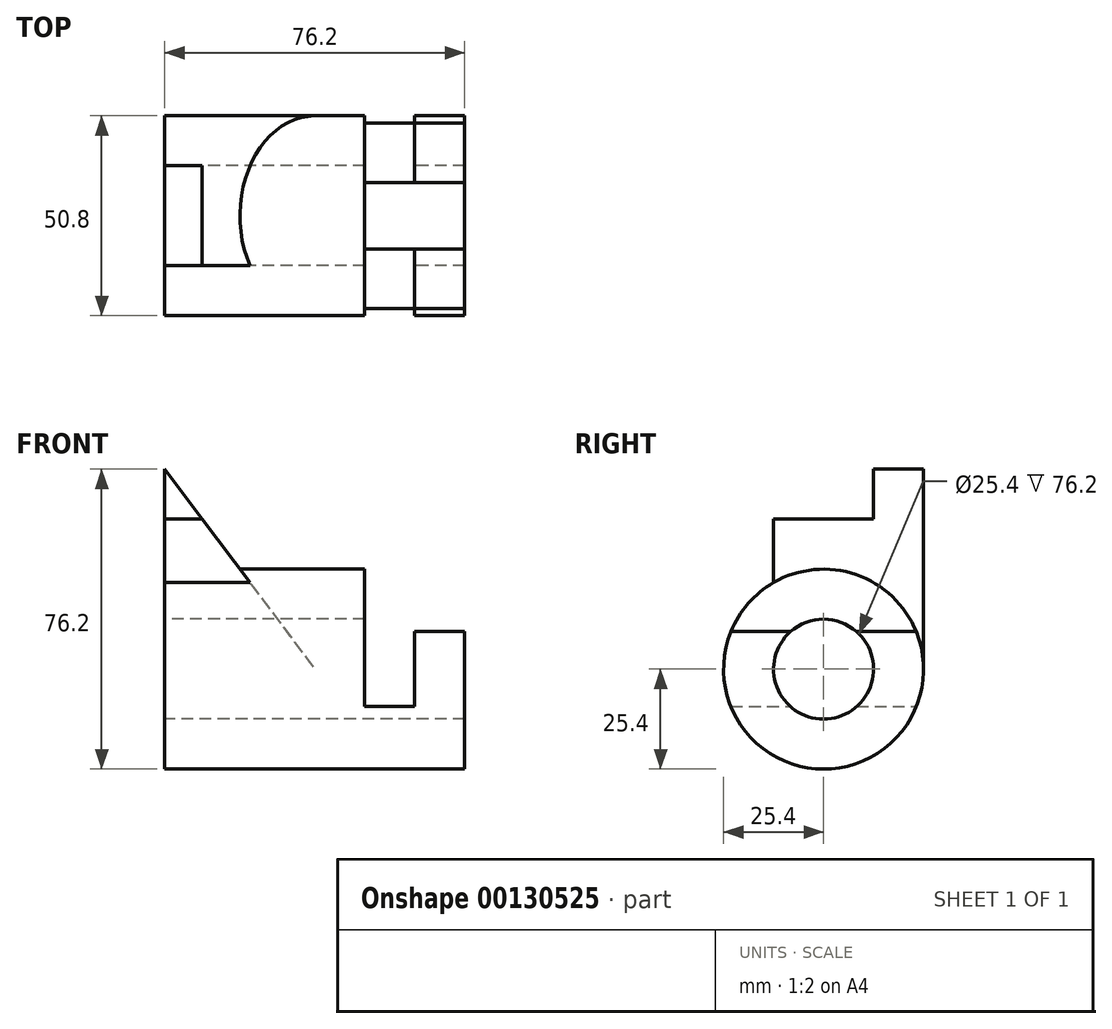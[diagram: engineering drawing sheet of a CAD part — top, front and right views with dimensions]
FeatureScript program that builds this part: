
annotation { "Feature Type Name" : "Feature", "Feature Type Description" : "" }
export const myFeature = defineFeature(function(context is Context, id is Id, definition is map)
    precondition{}
    {
        {
            var Q0;
            Q0=qCreatedBy(makeId("Right.planeOp"),FACE);
            var sketch = newSketch(context, id + "F0", { "sketchPlane" : qUnion([Q0])});
            skCircle(sketch, "E0", {"center": v(0, 0) * mm, "radius": 12.7 * mm});
            skCircle(sketch, "E1", {"center": v(0, 0) * mm, "radius": 25.4 * mm});
            skSolve(sketch);
        }
        {
            var Q0;
            Q0=makeQuery(id+"F0.imprint","IMPRINT",FACE,{"disambiguationData":[TD([[makeQuery(id+"F0.imprint","IMPRINT",EDGE,{"derivedFrom":sQuery(id+"F0.wireOp",EDGE,"E0")}),-1.0]])]});
            extrude(context, id + "F1", {"entities" : qUnion([Q0]), "depth" : 76.2 * mm});
        }
        {
            var Q0;
            Q0=qCreatedBy(makeId("Front.planeOp"),FACE);
            var sketch = newSketch(context, id + "F2", { "sketchPlane" : qUnion([Q0])});
            skLineSegment(sketch, "E2", {"start": v(50.8, 25.4) * mm, "end": v(50.8, -9.53) * mm});
            skLineSegment(sketch, "E3", {"start": v(50.8, -9.53) * mm, "end": v(63.5, -9.52) * mm});
            skLineSegment(sketch, "E4", {"start": v(63.5, -9.52) * mm, "end": v(63.5, 9.53) * mm});
            skLineSegment(sketch, "E5", {"start": v(63.5, 9.53) * mm, "end": v(76.2, 9.53) * mm});
            skLineSegment(sketch, "E6", {"start": v(76.2, 9.53) * mm, "end": v(76.2, 25.4) * mm});
            skLineSegment(sketch, "E7", {"start": v(76.2, 25.4) * mm, "end": v(50.8, 25.4) * mm});
            skLineSegment(sketch, "E8", {"start": v(25.4, 25.4) * mm, "end": v(76.2, 25.4) * mm});
            skLineSegment(sketch, "E9", {"start": v(76.2, -25.4) * mm, "end": v(0, -25.4) * mm});
            skSolve(sketch);
        }
        {
            var Q0;
            Q0=makeQuery(id+"F0.imprint","IMPRINT",FACE,{"disambiguationData":[TD([[makeQuery(id+"F0.imprint","IMPRINT",EDGE,{"derivedFrom":sQuery(id+"F0.wireOp",EDGE,"E0")}),1.0]])]});
            extrude(context, id + "F3", {"entities" : qUnion([Q0]), "operationType" : NewBodyOperationType.REMOVE, "depth" : 76.2 * mm});
        }
        {
            var Q0;
            Q0=qCreatedBy(makeId("Front.planeOp"),FACE);
            var sketch = newSketch(context, id + "F4", { "sketchPlane" : qUnion([Q0])});
            skLineSegment(sketch, "E10", {"start": v(0, 0) * mm, "end": v(0, 50.8) * mm});
            skLineSegment(sketch, "E11", {"start": v(0, 50.8) * mm, "end": v(38.1, 0) * mm});
            skLineSegment(sketch, "E12", {"start": v(0, 0) * mm, "end": v(38.1, 0) * mm});
            skSolve(sketch);
        }
        {
            var Q0;
            Q0 = qSketchRegion(id + "F2", true);
            extrude(context, id + "F5", {"entities" : qUnion([Q0]), "operationType" : NewBodyOperationType.REMOVE, "endBound" : BoundingType.SYMMETRIC, "depth" : 50.8 * mm});
        }
        {
            var Q0;
            Q0=makeQuery(id+"F4.imprint","IMPRINT",FACE,{"disambiguationData":[TD([[makeQuery(id+"F4.imprint","IMPRINT",EDGE,{"derivedFrom":sQuery(id+"F4.wireOp",EDGE,"E10")}),-1.0]])]});
            extrude(context, id + "F6", {"entities" : qUnion([Q0]), "operationType" : NewBodyOperationType.ADD, "oppositeDirection" : true, "depth" : 25.4 * mm});
        }
        {
            var Q0;
            Q0 = qSketchRegion(id + "F4", true);
            extrude(context, id + "F7", {"entities" : qUnion([Q0]), "operationType" : NewBodyOperationType.ADD, "depth" : 12.7 * mm});
        }
        {
            var Q0;
            Q0=qCreatedBy(makeId("Right.planeOp"),FACE);
            var sketch = newSketch(context, id + "F8", { "sketchPlane" : qUnion([Q0])});
            skLineSegment(sketch, "E13.bottom", {"start": v(-12.7, 38.1) * mm, "end": v(12.7, 38.1) * mm});
            skLineSegment(sketch, "E13.top", {"start": v(-12.7, 50.8) * mm, "end": v(12.7, 50.8) * mm});
            skLineSegment(sketch, "E13.left", {"start": v(-12.7, 38.1) * mm, "end": v(-12.7, 50.8) * mm});
            skLineSegment(sketch, "E13.right", {"start": v(12.7, 38.1) * mm, "end": v(12.7, 50.8) * mm});
            skSolve(sketch);
        }
        {
            var Q0;
            Q0 = qSketchRegion(id + "F8", true);
            extrude(context, id + "F9", {"entities" : qUnion([Q0]), "operationType" : NewBodyOperationType.REMOVE, "depth" : 25.4 * mm});
        }
        {
            var Q0;
            Q0=makeQuery(id+"F0.imprint","IMPRINT",FACE,{"disambiguationData":[TD([[makeQuery(id+"F0.imprint","IMPRINT",EDGE,{"derivedFrom":sQuery(id+"F0.wireOp",EDGE,"E0")}),1.0]])]});
            extrude(context, id + "F10", {"entities" : qUnion([Q0]), "operationType" : NewBodyOperationType.REMOVE, "depth" : 50.8 * mm});
        }
    });
